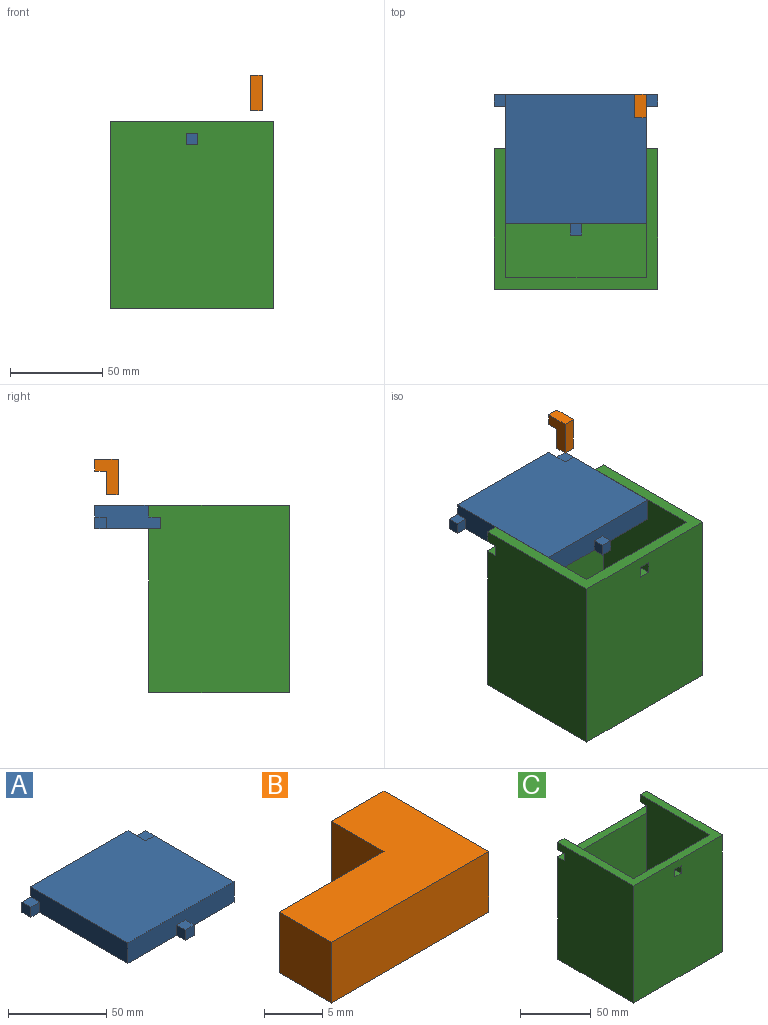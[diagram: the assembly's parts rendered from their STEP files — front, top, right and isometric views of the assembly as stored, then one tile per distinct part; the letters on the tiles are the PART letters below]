
ASSEMBLY  parts=3 mates=2
PART A: 18 faces, bbox 88.9x76.2x12.7 mm
  f0: plane 76.2x12.7mm, normal (0,-1,0), area 927.4mm2, adj f3,f4,f6,f7,f14,f15,f17
  f1: plane 12.7x12.7mm, normal (1,0,0), area 121mm2, adj f2,f5,f6,f7,f8,f10
  f2: plane 88.9x12.7mm, normal (0,1,0), area 1008.1mm2, adj f1,f3,f6,f7,f9,f10,f11,f13
  f3: plane 69.85x12.7mm, normal (-1,0,0), area 846.8mm2, adj f0,f2,f6,f7,f12,f13
  f4: plane 57.15x12.7mm, normal (1,0,0), area 725.8mm2, adj f0,f5,f6,f7
  f5: plane 12.7x6.35mm, normal (0,1,0), area 80.6mm2, adj f1,f4,f6,f7
  f6: plane 76.2x69.85mm, normal (0,0,1), area 5241.9mm2, adj f0,f1,f2,f3,f4,f5
  f7: plane 88.9x76.2mm, normal (0,0,-1), area 5403.2mm2, adj f0,f1,f2,f3,f4,f5,f8,f9
  f8: plane 12.7x6.35mm, normal (0,-1,0), area 80.6mm2, adj f1,f7,f9,f10
  f9: plane 6.35x6.35mm, normal (1,0,0), area 40.3mm2, adj f2,f7,f8,f10
  f10: plane 12.7x6.35mm, normal (0,0,1), area 80.6mm2, adj f1,f2,f8,f9
  f11: plane 6.35x6.35mm, normal (-1,0,0), area 40.3mm2, adj f2,f7,f12,f13
  f12: plane 6.35x6.35mm, normal (0,-1,0), area 40.3mm2, adj f3,f7,f11,f13
  f13: plane 6.35x6.35mm, normal (0,0,1), area 40.3mm2, adj f2,f3,f11,f12
  f14: plane 6.35x6.35mm, normal (1,0,0), area 40.3mm2, adj f0,f7,f16,f17
  f15: plane 6.35x6.35mm, normal (-1,0,0), area 40.3mm2, adj f0,f7,f16,f17
  f16: plane 6.35x6.35mm, normal (0,-1,0), area 40.3mm2, adj f7,f14,f15,f17
  f17: plane 6.35x6.35mm, normal (0,0,1), area 40.3mm2, adj f0,f14,f15,f16
PART B: 8 faces, bbox 19.1x12.7x6.4 mm
  f0: plane 6.35x6.35mm, normal (-1,0,0), area 40.3mm2, adj f1,f5,f6,f7
  f1: plane 19.05x6.35mm, normal (0,-1,0), area 121mm2, adj f0,f2,f6,f7
  f2: plane 12.7x6.35mm, normal (1,0,0), area 80.6mm2, adj f1,f3,f6,f7
  f3: plane 6.35x6.35mm, normal (0,1,0), area 40.3mm2, adj f2,f4,f6,f7
  f4: plane 6.35x6.35mm, normal (-1,0,0), area 40.3mm2, adj f3,f5,f6,f7
  f5: plane 12.7x6.35mm, normal (0,1,0), area 80.6mm2, adj f0,f4,f6,f7
  f6: plane 19.05x12.7mm, normal (0,0,1), area 161.3mm2, adj f0,f1,f2,f3,f4,f5
  f7: plane 19.05x12.7mm, normal (0,0,-1), area 161.3mm2, adj f0,f1,f2,f3,f4,f5
PART C: 22 faces, bbox 88.9x76.2x101.6 mm
  f0: plane 6.35x6.35mm, normal (0,1,0), area 40.3mm2, adj f3,f8,f11,f14
  f1: plane 88.9x88.9mm, normal (0,1,0), area 7903.2mm2, adj f2,f4,f11,f15
  f2: plane 101.6x76.2mm, normal (-1,0,0), area 7701.6mm2, adj f1,f3,f4,f9,f10,f13,f15,f16
  f3: plane 88.9x76.2mm, normal (0,0,1), area 1451.6mm2, adj f0,f2,f6,f7,f8,f9,f10,f11
  f4: plane 88.9x76.2mm, normal (0,0,-1), area 6774.2mm2, adj f1,f2,f10,f11
  f5: plane 82.55x76.2mm, normal (0,-1,0), area 6290.3mm2, adj f6,f8,f12,f15
  f6: plane 95.25x69.85mm, normal (1,0,0), area 6088.7mm2, adj f3,f5,f7,f9,f12,f13,f16
  f7: plane 95.25x76.2mm, normal (0,1,0), area 7217.7mm2, adj f3,f6,f8,f12,f18,f19,f20,f21
  f8: plane 95.25x69.85mm, normal (-1,0,0), area 6088.7mm2, adj f0,f3,f5,f7,f12,f14,f17
  f9: plane 6.35x6.35mm, normal (0,1,0), area 40.3mm2, adj f2,f3,f6,f16
  f10: plane 101.6x88.9mm, normal (0,-1,0), area 8991.9mm2, adj f2,f3,f4,f11,f18,f19,f20,f21
  f11: plane 101.6x76.2mm, normal (1,0,0), area 7701.6mm2, adj f0,f1,f3,f4,f10,f14,f15,f17
  f12: plane 76.2x63.5mm, normal (0,0,1), area 4838.7mm2, adj f5,f6,f7,f8
  f13: plane 6.35x6.35mm, normal (0,1,0), area 40.3mm2, adj f2,f6,f15,f16
  f14: plane 6.35x6.35mm, normal (0,0,-1), area 40.3mm2, adj f0,f8,f11,f17
  f15: plane 88.9x6.35mm, normal (0,0,1), area 564.5mm2, adj f1,f2,f5,f11,f13,f17
  f16: plane 6.35x6.35mm, normal (0,0,-1), area 40.3mm2, adj f2,f6,f9,f13
  f17: plane 6.35x6.35mm, normal (0,1,0), area 40.3mm2, adj f8,f11,f14,f15
  f18: plane 6.35x6.35mm, normal (1,0,0), area 40.3mm2, adj f7,f10,f19,f21
  f19: plane 6.35x6.35mm, normal (0,0,1), area 40.3mm2, adj f7,f10,f18,f20
  f20: plane 6.35x6.35mm, normal (-1,0,0), area 40.3mm2, adj f7,f10,f19,f21
  f21: plane 6.35x6.35mm, normal (0,0,-1), area 40.3mm2, adj f7,f10,f18,f20
PLACE A rot(axis=(0,0,1),0deg) t=(70.66,231.16,88.9)mm
PLACE B rot(axis=(0,-1,0),90deg) t=(82.55,248.1,60.84)mm
PLACE C at identity
MATE slider A.f0 <-> C.f7  axis (0,-1,0) through (82.55,35.71,101.6)mm
MATE slider B.f2 <-> A.f6  axis (0,0,-1) through (76.2,92.86,126.51)mm
